# Revit family: GGL_Integra_v_1.01
name_source: partatom
category: Окна
revit_build: Autodesk Revit 2017 (Build: 20160225_1515(x64)
units: mm (PartAtom-declared; Revit-internal decimal feet)

## family parameters
Всегда вертикально = Нет
Общий = Нет
Основа = Крыша
При загрузке вырезать с полостями = Нет
Точка расчета площади = Нет

## types (1)
- Default
    Allowed Roof Slope = 15°-90°
    Angle = -19.99°
    BIMobject Category = Roof Window
    Chain(box)-length = 200 мм
    Date of publishing = 6/27/2013
    Design country = Denmark
    Edition number = 1
    Emergency Exit = Нет
    Frame Area = 1.78
    Function = Electrical pivot hung roof window
    GlazingAreaFraction = 0.36
    IFC Classification = Window
    Installation instructions = http://www.velux.co.uk
    Light transmittance = 0.79
    Manufacturer URL = www.velux.com
    Manufacturer country = Denmark
    Material main = Wood
    Material secondary = Glass 73Q + ISD 0000
    NBS Reference = 59-72
    NBS Reference Description = Roof Window Units
    Name of the object = New Generation - GGL Integra
    Offset from Roof = 169 мм
    Open Window = Да
    Operation Mode = Electrical
    Panel Offset = -119 мм
    Perimeter Glazing = 5.13
    Perimeter Window = 5.88
    Placement Height = 0 мм
    Product SKU = gglint101
    Product data url = http://www.velux.co.uk
    Product family = Center pivot hung roof window
    Product group = GGL Integra 1.01
    Roof Slope = 45.00°
    Sound Insulation db = 35
    Square Reveal Length = 150 мм
    Thermal Transmittance(frame) = 1.3
    Thermal bridge = 0.09
    Thermal bridge(glazing) = 0.057
    ThermalTransmittance = 1.3
    ThermalTransmittance - Glazing = 1.1
    UNSPC Category = Roofing accessories
    UNSPC code = 301516
    URL = http://file-system.ru
    Uniclass 1.4 Code = JL11
    Uniclass 1.4 Description = Rooflights/Roof windows
    Uniclass 2.0 Code = PR-59-72
    Uniclass 2.0 Description = Roof Window Units
    Warranty Years = 5 (10 with BDX)
    Window Area = 2.14
    g-value = 0.64
    Высота = 1600 мм
    Группа модели = New Generation - GGL Integra
    Изготовитель = VELUX A/S
    Код по классификатору = B3020110
    Ширина = 1340 мм

## geometry (parser evidence)
native form markers: Blend x49, Sweep x4
no freeform markers — native parametric forms only
